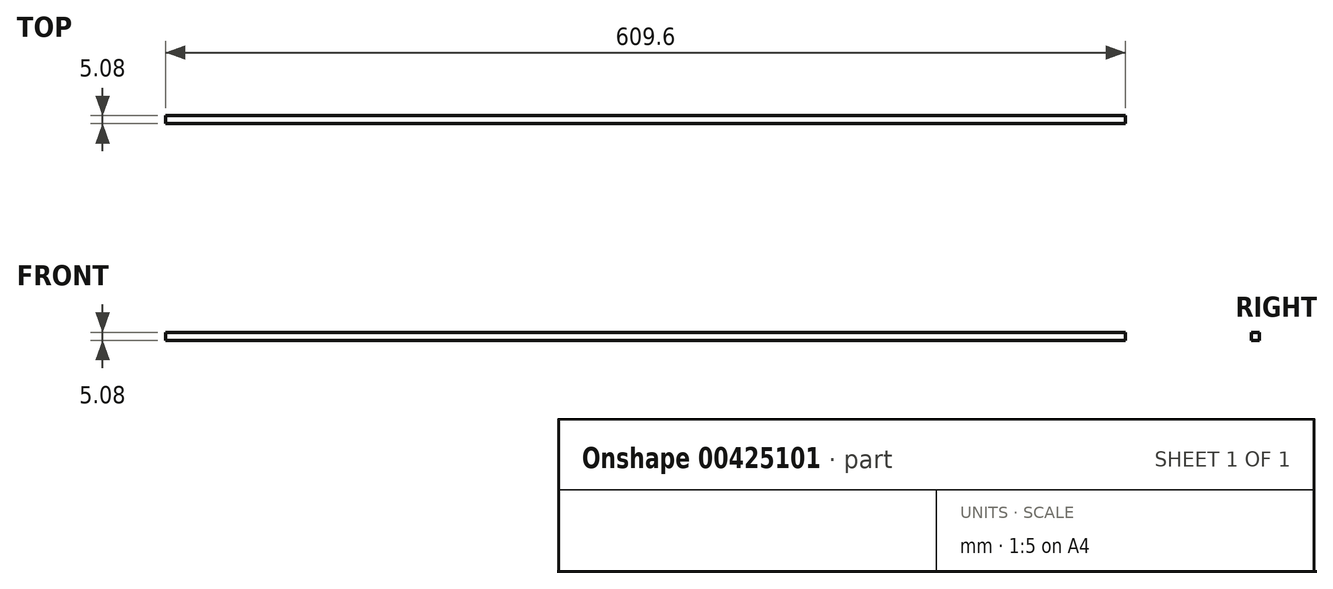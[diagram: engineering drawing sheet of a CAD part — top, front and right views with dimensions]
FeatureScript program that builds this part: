
annotation { "Feature Type Name" : "Feature", "Feature Type Description" : "" }
export const myFeature = defineFeature(function(context is Context, id is Id, definition is map)
    precondition{}
    {
        {
            var Q0;
            Q0=qCreatedBy(makeId("Front.planeOp"),FACE);
            var sketch = newSketch(context, id + "F0", { "sketchPlane" : qUnion([Q0])});
            skLineSegment(sketch, "E0.bottom", {"start": v(289.93, -97.7) * mm, "end": v(-319.67, -97.7) * mm});
            skLineSegment(sketch, "E0.top", {"start": v(289.93, -102.77) * mm, "end": v(-319.67, -102.77) * mm});
            skLineSegment(sketch, "E0.left", {"start": v(289.93, -97.7) * mm, "end": v(289.93, -102.77) * mm});
            skLineSegment(sketch, "E0.right", {"start": v(-319.67, -97.7) * mm, "end": v(-319.67, -102.77) * mm});
            skSolve(sketch);
        }
        {
            var Q0;
            Q0 = qSketchRegion(id + "F0", true);
            extrude(context, id + "F1", {"entities" : qUnion([Q0]), "depth" : 5.08 * mm});
        }
    });
